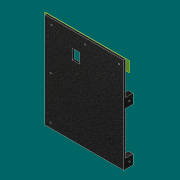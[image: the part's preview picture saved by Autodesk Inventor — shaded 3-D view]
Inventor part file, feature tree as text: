
AUTODESK INVENTOR PART (.ipt)
format: ipt  version: 2019 (Build 230136000, 136)  size: 204,800 bytes
history: native  units: mm
features: reference x17, sketch x12, extrude x10, other x3, plane x1
ambient origin geometry x8: Origin, YZ Plane, XZ Plane, XY Plane, X Axis, Y Axis, Z Axis, Center Point
bodies: Solid1 (feature_tree)
feature tree (43):
  plane  "Work Plane1"
  extrude  "Extrusion1"  Depth=8.0mm
  sketch  "Sketch2"  dims[d4=10.0mm d6=1.5mm]
  sketch  "Sketch3"  dims[d7=5.0mm d8=0.0mm d9=8.0mm]
  extrude  "Extrusion2"  Depth=10.0mm
  extrude  "Extrusion3"  Depth=8.0mm
  extrude  "Extrusion4"  Depth=10.0mm
  extrude  "Extrusion5"  Depth=10.0mm
  extrude  "Extrusion6"  Depth=8.0mm
  extrude  "Extrusion7"  Depth=5.0mm
  extrude  "Extrusion8"  Depth=5.0mm
  extrude  "Extrusion9"  Depth=10.0mm
  extrude  "Extrusion10"  Depth=5.0mm TaperAngle=0.0deg
  sketch  "Sketch1"  dims[d0=2.0mm d1=0.0mm d3=8.0mm]
  reference  "Reference1"
  reference  "Reference2"
  reference  "Reference3"
  reference  "Reference4"
  reference  "Reference5"
  reference  "Reference6"
  reference  "Reference7"
  reference  "Reference8"
  reference  "Reference9"
  sketch  "Sketch4"  dims[d10=10.0mm d12=1.5mm]
  reference  "Reference10"
  reference  "Reference11"
  reference  "Reference12"
  reference  "Reference13"
  sketch  "Sketch5"  dims[d13=5.0mm d14=0.0mm d15=10.0mm]
  sketch  "Sketch6"  dims[d16=8.0mm d18=1.5mm]
  sketch  "Sketch7"  dims[d19=5.0mm d20=0.0mm d22=1.5mm]
  reference  "Reference14"
  sketch  "Sketch8"  dims[d25=4.0mm d26=5.0mm]
  sketch  "Sketch9"  dims[d27=8.0mm d28=10.0mm]
  reference  "Reference15"
  reference  "Reference16"
  reference  "Reference17"
  sketch  "Sketch10"  dims[d29=8.0mm d30=5.0mm d31=0.0mm]
  sketch  "Sketch11"  dims[d32=5.0mm d33=0.0mm]
  sketch  "Sketch12"  dims[d35=8.0mm d36=10.0mm d38=1.5mm d39=5.0mm d40=0.0mm d41=10.0mm d42=8.0mm d43=0.0mm d44=5.0mm d45=10.0mm d46=5.0mm d47=10.0mm d48=8.0mm d49=0.0mm d51=1.5mm d52=5.0mm d53=0.0mm]
  other  "Ensamblaje Reloj LCD 16x2.iam"
  other  "Before:1"
  other  "Down:1"
